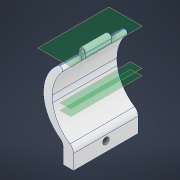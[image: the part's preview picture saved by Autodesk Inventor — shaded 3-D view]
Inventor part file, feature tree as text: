
AUTODESK INVENTOR PART (.ipt)
format: ipt  version: 2021 (Build 250183000, 183)  size: 200,704 bytes
history: native  units: in
note: dims shown in document units (in); Inventor stores cm internally (conversion verified against a paired STEP export)
features: extrude x5, fillet x5, sketch x5, plane x3, split x2, hole x1
ambient origin geometry x8: Origin, YZ Plane, XZ Plane, XY Plane, X Axis, Y Axis, Z Axis, Center Point
bodies: Solid1 (feature_tree)
feature tree (21):
  extrude  "Extrusion1"  Depth=3.937in TaperAngle=0.0deg
  extrude  "Extrusion2"  Depth=0.1969in
  plane  "Work Plane1"
  extrude  "Extrusion3"  Depth=3.937in TaperAngle=0.0deg
  extrude  "Extrusion4"  Depth=0.4724in TaperAngle=0.0deg
  extrude  "Extrusion5"  Depth=1.5748in TaperAngle=0.0deg
  hole  "Hole1"  [1 undecoded]
  fillet  "Fillet1"  Radius=0.3937in
  fillet  "Fillet2"  Radius=0.1181in
  fillet  "Fillet3"  Radius=2.3622in
  fillet  "Fillet4"  Radius=1.1811in
  fillet  "Fillet5"  Radius=0.1575in
  plane  "Work Plane2"
  plane  "Work Plane3"
  split  "Split1"
  split  "Split2"
  sketch  "Sketch1"  dims[d1=3.937in d2=2.3622in d3=1.1811in d5=0.4724in d6=3.937in d7=1.1811in d8=0.3937in d9=3.937in d10=0.0in]
  sketch  "Sketch2"  dims[d11=0.2756in d12=0.1969in]
  sketch  "Sketch3"  dims[d13=0.3937in d14=3.937in d15=0.0in]
  sketch  "Sketch5"  dims[d17=0.4724in d18=0.0in d20=0.4724in d21=0.0in]
  sketch  "Sketch6"  dims[d22=0.2756in d23=1.5748in d24=0.0in d25=0.5906in d26=0.3937in d27=0.3937in d28=0.2362in d29=0.1575in d30=0.0787in d31=90.0deg d32=0.315in d33=0.8108in d34=0.1181in d37=2.3622in d38=1.1811in d39=0.1575in d40=0.1181in d41=1.1811in d42=0.315in d43=0.4724in d44=0.6299in d45=0.4724in d46=1.1811in d47=-3.3465in d48=-2.9528in]
note: 1 required parameter value undecoded (feature->parameter linkage not recoverable at this tier; creation-order binding heuristic only, values carry confidence <= 0.55)
